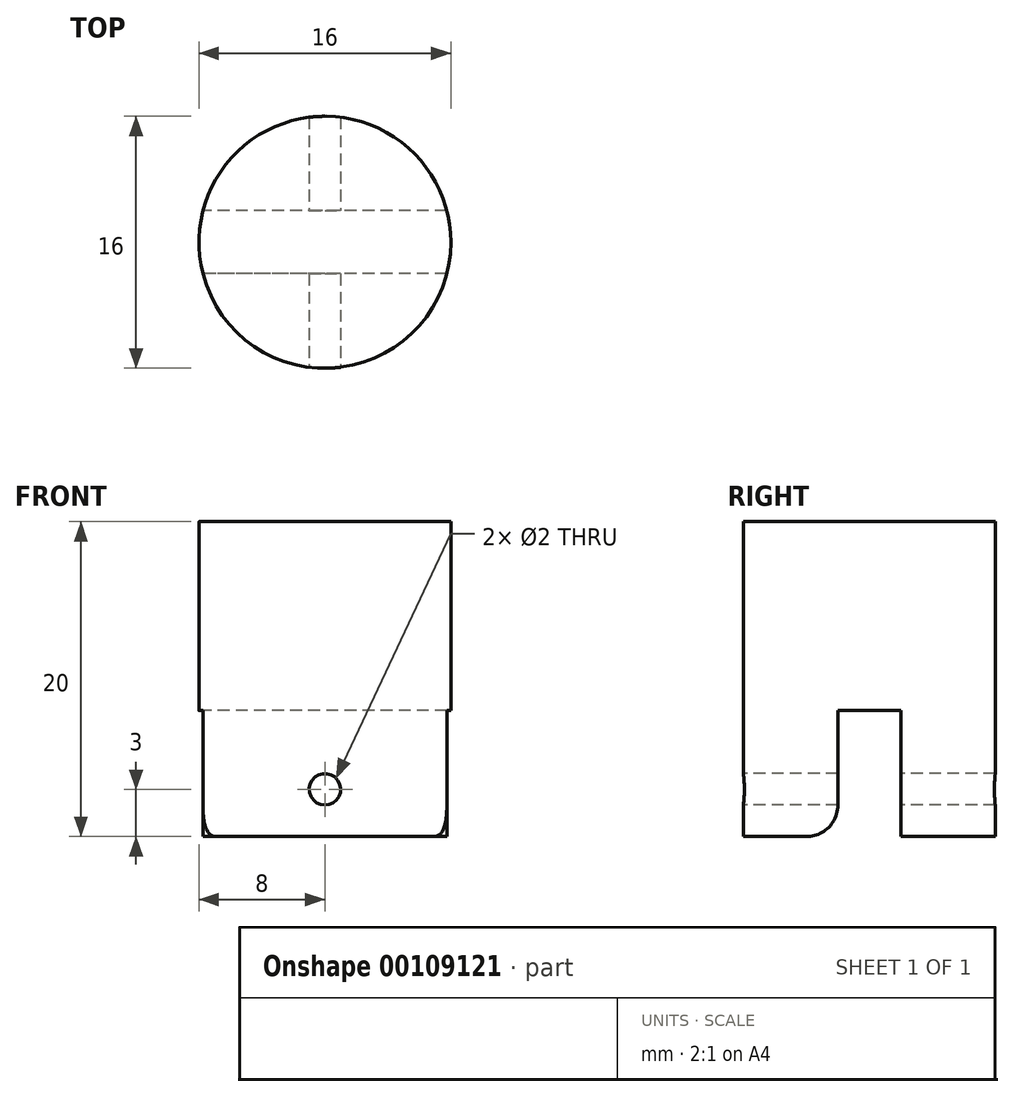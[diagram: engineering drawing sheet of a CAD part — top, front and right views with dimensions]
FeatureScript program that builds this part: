
annotation { "Feature Type Name" : "Feature", "Feature Type Description" : "" }
export const myFeature = defineFeature(function(context is Context, id is Id, definition is map)
    precondition{}
    {
        {
            var Q0;
            Q0=qCreatedBy(makeId("Top.planeOp"),FACE);
            var sketch = newSketch(context, id + "F0", { "sketchPlane" : qUnion([Q0])});
            skCircle(sketch, "E0", {"center": v(0, 0) * mm, "radius": 8 * mm});
            skSolve(sketch);
        }
        {
            var Q0;
            Q0=qSketchRegion(id+"F0",true);
            extrude(context, id + "F1", {"entities" : qUnion([Q0]), "depth" : 20 * mm});
        }
        {
            var Q0;
            Q0=makeQuery(id+"F1.opExtrude","CAP_FACE",FACE,{"disambiguationData":[OSD([sQuery(id+"F0.wireOp",EDGE,"E0")])],"isStart":true});
            var sketch = newSketch(context, id + "F2", { "sketchPlane" : qUnion([Q0])});
            skPoint(sketch, "E1.middle", {"position": v(0, 0) * mm});
            skLineSegment(sketch, "E2.bottom", {"start": v(9.5, -2) * mm, "end": v(-9.5, -2) * mm});
            skLineSegment(sketch, "E2.top", {"start": v(9.5, 2) * mm, "end": v(-9.5, 2) * mm});
            skLineSegment(sketch, "E2.left", {"start": v(9.5, -2) * mm, "end": v(9.5, 2) * mm});
            skLineSegment(sketch, "E2.right", {"start": v(-9.5, -2) * mm, "end": v(-9.5, 2) * mm});
            skSolve(sketch);
        }
        {
            var Q0;
            Q0=qSketchRegion(id+"F2",true);
            extrude(context, id + "F3", {"entities" : qUnion([Q0]), "operationType" : NewBodyOperationType.REMOVE, "oppositeDirection" : true, "depth" : 8 * mm});
        }
        {
            var Q0;
            Q0=qCreatedBy(makeId("Front.planeOp"),FACE);
            var sketch = newSketch(context, id + "F4", { "sketchPlane" : qUnion([Q0])});
            skCircle(sketch, "E3", {"center": v(0, 3) * mm, "radius": 1 * mm});
            skSolve(sketch);
        }
        {
            var Q0;
            Q0=qSketchRegion(id+"F4",true);
            extrude(context, id + "F5", {"entities" : qUnion([Q0]), "operationType" : NewBodyOperationType.REMOVE, "endBound" : BoundingType.SYMMETRIC, "oppositeDirection" : true, "depth" : 16 * mm});
        }
        {
            var Q0;
            Q0=makeQuery(id+"F3.boolean.opBoolean","COPY",EDGE,{"derivedFrom":makeQuery(id+"F3.opExtrude","CAP_EDGE",EDGE,{"disambiguationData":[OSD([sQuery(id+"F2.wireOp",EDGE,"E2.top")])],"isStart":true})});
            var Q1;
            Q1=makeQuery(id+"F3.boolean.opBoolean","COPY",EDGE,{"derivedFrom":makeQuery(id+"F3.opExtrude","CAP_EDGE",EDGE,{"disambiguationData":[OSD([sQuery(id+"F2.wireOp",EDGE,"E2.bottom")])],"isStart":true})});
            fillet(context, id + "F6", {"entities" : qUnion([Q0, Q1]), "radius" : 2 * mm, "tangentPropagation" : true, "allowEdgeOverflow" : false});
        }
    });
